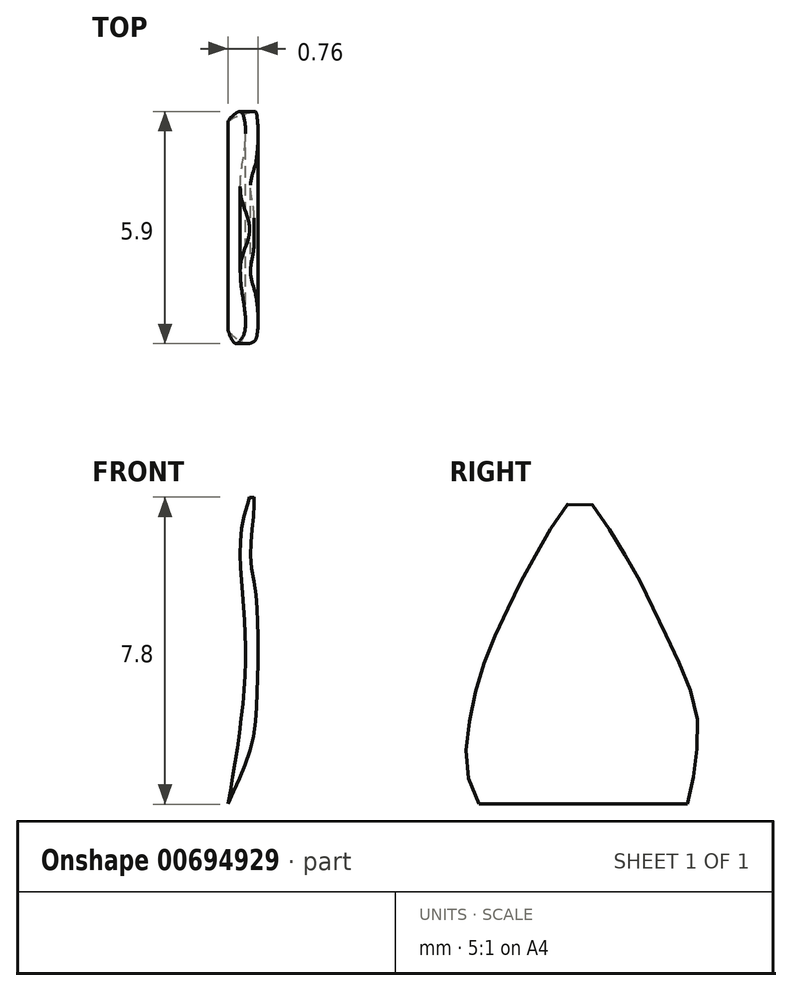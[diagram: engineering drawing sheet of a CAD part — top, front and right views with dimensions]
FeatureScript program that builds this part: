
annotation { "Feature Type Name" : "Feature", "Feature Type Description" : "" }
export const myFeature = defineFeature(function(context is Context, id is Id, definition is map)
    precondition{}
    {
        {
            var Q0;
            Q0=qCreatedBy(makeId("Right.planeOp"),FACE);
            var sketch = newSketch(context, id + "F0", { "sketchPlane" : qUnion([Q0])});
            skPoint(sketch, "E0", {"position": v(0, 0) * mm});
            skFitSpline(sketch, "E1", {"points": [v(0, 5.23) * mm, v(0.74, 4.49) * mm, v(1.52, 3.16) * mm, v(2.08, 2) * mm, v(2.94, 0) * mm, v(2.98, -1.36) * mm, v(2.4, -3.22) * mm, v(0, -4.05) * mm, v(-1.77, -3.55) * mm, v(-2.74, -2.08) * mm, v(-2.84, -1.02) * mm, v(-2.44, 0.9) * mm, v(-1.92, 2.12) * mm, v(-1.48, 3.06) * mm, v(-0.9, 4.09) * mm, v(0, 5.23) * mm]});
            skSolve(sketch);
        }
        {
            var Q0;
            Q0=makeQuery(id+"F0.imprint","IMPRINT",FACE,{"disambiguationData":[TD([[makeQuery(id+"F0.imprint","IMPRINT",EDGE,{"derivedFrom":sQuery(id+"F0.wireOp",EDGE,"E1")}),-1.0]])]});
            extrude(context, id + "F1", {"entities" : qUnion([Q0]), "oppositeDirection" : true, "depth" : 1 * mm, "offsetDistance" : 25 * mm});
        }
        {
            var Q0;
            Q0=qCreatedBy(makeId("Front.planeOp"),FACE);
            var sketch = newSketch(context, id + "F2", { "sketchPlane" : qUnion([Q0])});
            skFitSpline(sketch, "E2", {"points": [v(-0.31, 5.47) * mm, v(-0.23, 5.36) * mm, v(-0.28, 3.95) * mm, v(-0.18, 3.05) * mm, v(-0.09, 1.5) * mm, v(-0.13, -0.26) * mm, v(-0.4, -1.52) * mm, v(-1.15, -3.92) * mm, v(-0.24, -4.3) * mm, v(0.96, -3.35) * mm, v(1.1, 3.79) * mm, v(1.2, 5.59) * mm, v(-0.31, 5.47) * mm]});
            skFitSpline(sketch, "E3", {"points": [v(-0.94, 5.45) * mm, v(-0.31, 5.47) * mm, v(-0.45, 4.7) * mm, v(-0.5, 2.93) * mm, v(-0.4, 1.56) * mm, v(-0.53, -0.56) * mm, v(-1.23, -4.13) * mm, v(-1.36, -4.18) * mm, v(-2.4, -3.72) * mm, v(-1.6, 5.24) * mm, v(-0.94, 5.45) * mm]});
            skSolve(sketch);
        }
        {
            var Q0;
            Q0=qSketchRegion(id+"F2",true);
            extrude(context, id + "F3", {"entities" : qUnion([Q0]), "operationType" : NewBodyOperationType.REMOVE, "oppositeDirection" : true, "depth" : 8 * mm, "offsetDistance" : 25 * mm, "symmetric" : true});
        }
        {
            var Q0;
            Q0=makeQuery(id+"F1.opExtrude","SWEPT_BODY",BODY,{"disambiguationData":[OSD([sQuery(id+"F0.wireOp",EDGE,"E1")])]});
            transform(context, id + "F4", {"entities" : qUnion([Q0]), "transformType" : TransformType.TRANSLATION_3D, "dx" : 0 * mm, "dy" : 0 * mm, "dz" : 0 * mm, "makeCopy" : true});
        }
    });
